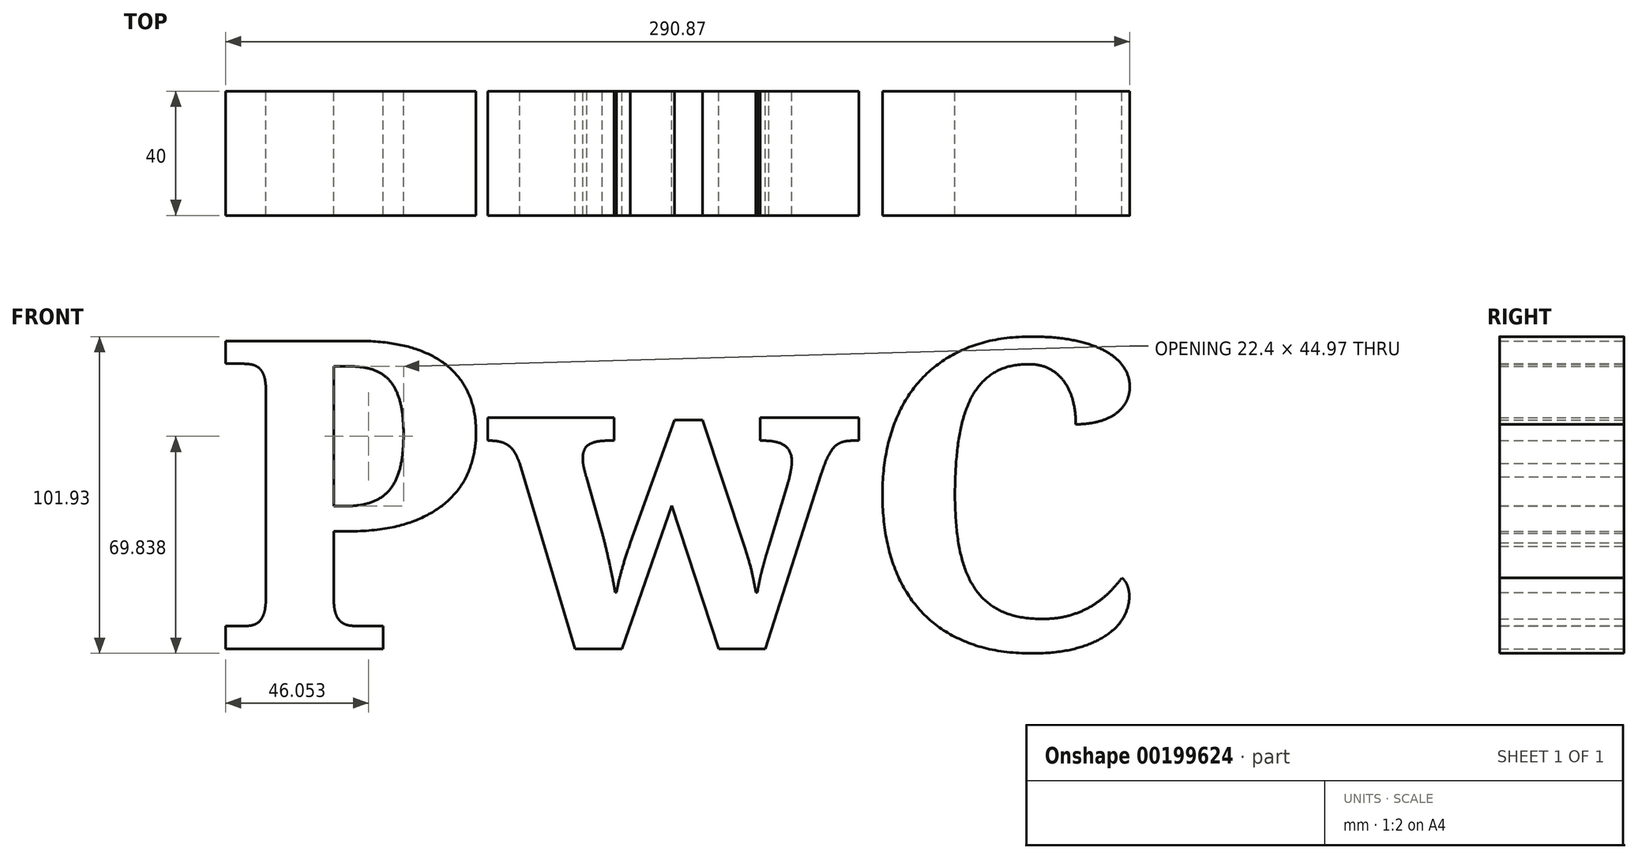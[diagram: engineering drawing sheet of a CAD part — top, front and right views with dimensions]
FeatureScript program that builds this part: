
annotation { "Feature Type Name" : "Feature", "Feature Type Description" : "" }
export const myFeature = defineFeature(function(context is Context, id is Id, definition is map)
    precondition{}
    {
        {
            var Q0;
            Q0=qCreatedBy(makeId("Front.planeOp"),FACE);
            var sketch = newSketch(context, id + "F0", { "sketchPlane" : qUnion([Q0])});
            skText(sketch, "E0", { "text": "PwC", "fontName": "NotoSerif-Bold.ttf"});
            const initialGuessF0  = {"E0": [-0.17097, -0.15538, 1, 0, 0.1]};
            skSetInitialGuess(sketch, initialGuessF0);
            skSolve(sketch);
        }
        {
            var Q0;
            Q0=qSketchRegion(id+"F0",true);
            extrude(context, id + "F1", {"entities" : qUnion([Q0]), "depth" : 40 * mm});
        }
    });
